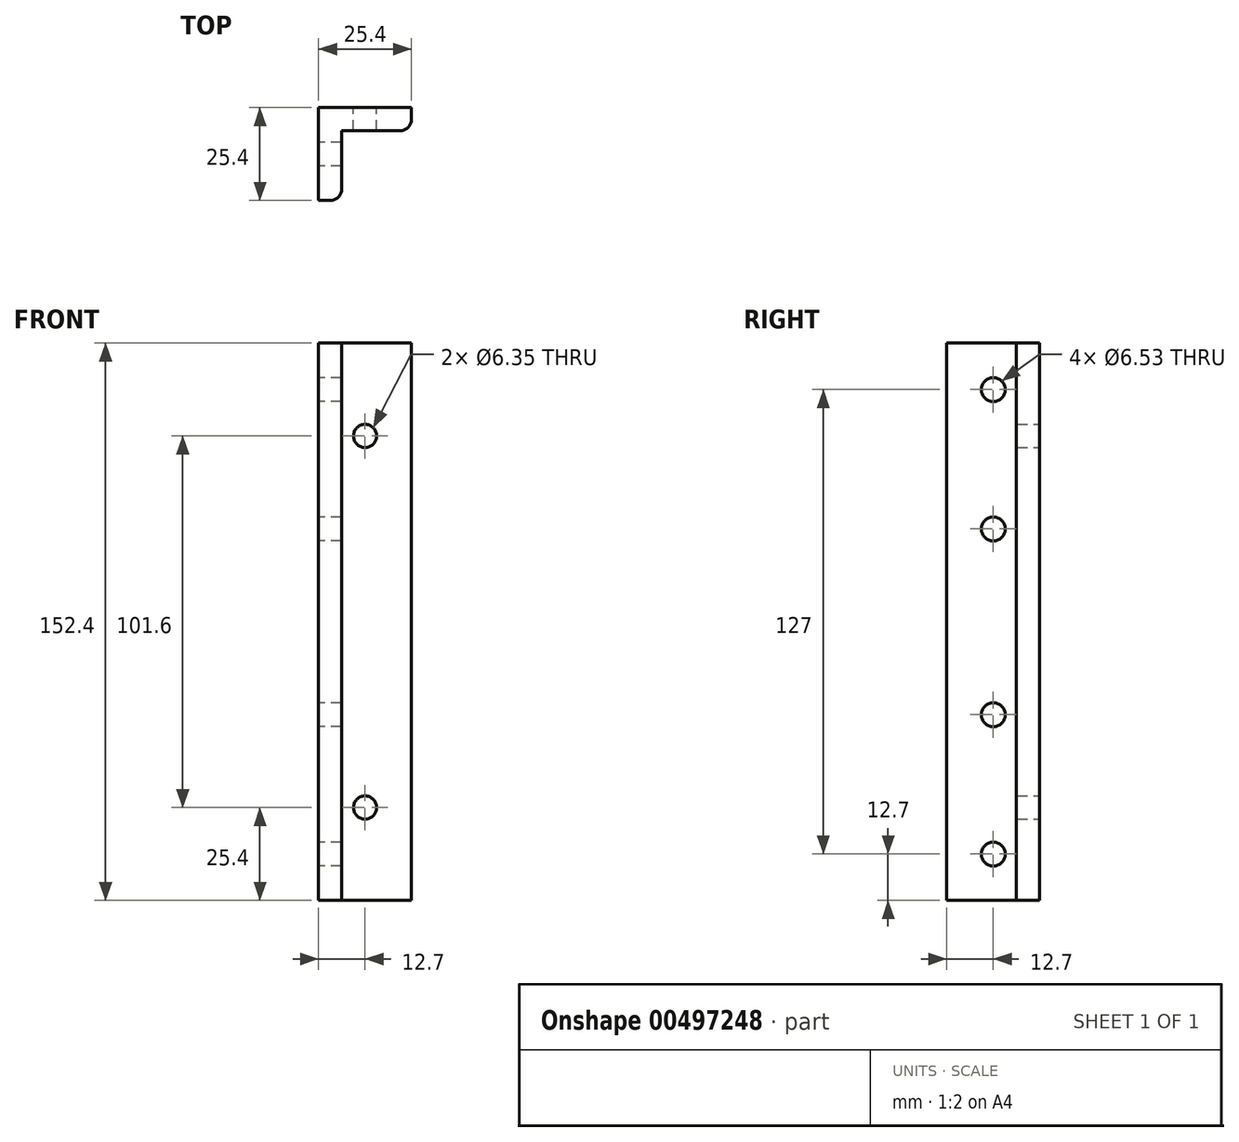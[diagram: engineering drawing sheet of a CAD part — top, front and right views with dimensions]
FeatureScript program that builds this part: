
annotation { "Feature Type Name" : "Feature", "Feature Type Description" : "" }
export const myFeature = defineFeature(function(context is Context, id is Id, definition is map)
    precondition{}
    {
        {
            var Q0;
            Q0=qCreatedBy(makeId("Top.planeOp"),FACE);
            var sketch = newSketch(context, id + "F0", { "sketchPlane" : qUnion([Q0])});
            skLineSegment(sketch, "E0", {"start": v(0, 0) * mm, "end": v(25.4, 0) * mm});
            skLineSegment(sketch, "E1", {"start": v(0, 0) * mm, "end": v(0, -25.4) * mm});
            skLineSegment(sketch, "E2", {"start": v(6.35, -19.05) * mm, "end": v(6.35, -6.35) * mm});
            skLineSegment(sketch, "E3", {"start": v(6.35, -6.35) * mm, "end": v(18.93, -6.35) * mm});
            skLineSegment(sketch, "E4", {"start": v(0, -25.4) * mm, "end": v(3.18, -25.4) * mm});
            skLineSegment(sketch, "E5", {"start": v(6.35, -22.23) * mm, "end": v(6.35, -19.05) * mm});
            skArc(sketch, "E6", {"start": v(3.18, -25.4) * mm, "mid": v(5.42, -24.47) * mm, "end": v(6.35, -22.23) * mm});
            skLineSegment(sketch, "E7", {"start": v(19.17, -6.35) * mm, "end": v(22.23, -6.35) * mm});
            skLineSegment(sketch, "E8", {"start": v(25.4, -3.17) * mm, "end": v(25.4, 0) * mm});
            skArc(sketch, "E9.trimOffspring", {"start": v(25.4, 0) * mm, "mid": v(25.4, 0) * mm, "end": v(25.4, 0) * mm});
            skLineSegment(sketch, "E10", {"start": v(18.93, -6.35) * mm, "end": v(19.17, -6.35) * mm});
            skArc(sketch, "E11", {"start": v(22.23, -6.35) * mm, "mid": v(24.47, -5.42) * mm, "end": v(25.4, -3.17) * mm});
            skPoint(sketch, "E12.orphan", {"position": v(6.35, -25.4) * mm});
            skPoint(sketch, "E13.orphan", {"position": v(25.4, -6.35) * mm});
            skSolve(sketch);
        }
        {
            var Q0;
            Q0 = qSketchRegion(id + "F0", true);
            extrude(context, id + "F1", {"entities" : qUnion([Q0]), "depth" : 152.4 * mm});
        }
        {
            var Q0;
            Q0=makeQuery(id+"F1.opExtrude","SWEPT_FACE",FACE,{"disambiguationData":[OSD([sQuery(id+"F0.wireOp",EDGE,"E1")])]});
            var sketch = newSketch(context, id + "F2", { "sketchPlane" : qUnion([Q0])});
            skPoint(sketch, "E14", {"position": v(12.7, 139.7) * mm});
            skPoint(sketch, "E15", {"position": v(12.7, 12.7) * mm});
            skPoint(sketch, "E16", {"position": v(12.7, 50.8) * mm});
            skPoint(sketch, "E17", {"position": v(12.7, 101.6) * mm});
            skSolve(sketch);
        }
        {
            var Q0;
            Q0=makeQuery(id+"F1.opExtrude","SWEPT_FACE",FACE,{"disambiguationData":[OSD([sQuery(id+"F0.wireOp",EDGE,"E0")])]});
            var sketch = newSketch(context, id + "F3", { "sketchPlane" : qUnion([Q0])});
            skPoint(sketch, "E18", {"position": v(-12.7, 127) * mm});
            skPoint(sketch, "E19", {"position": v(-12.7, 25.4) * mm});
            skSolve(sketch);
        }
        {
            var Q0;
            Q0=sQuery(id+"F3.wireOp",VERTEX,"E18");
            var Q1;
            Q1=sQuery(id+"F3.wireOp",VERTEX,"E19");
            var Q2;
            Q2=makeQuery(id+"F1.opExtrude","SWEPT_BODY",BODY,{"disambiguationData":[OSD([sQuery(id+"F0.wireOp",EDGE,"E0"),sQuery(id+"F0.wireOp",EDGE,"E1"),sQuery(id+"F0.wireOp",EDGE,"E2"),sQuery(id+"F0.wireOp",EDGE,"E3"),sQuery(id+"F0.wireOp",EDGE,"E4"),sQuery(id+"F0.wireOp",EDGE,"E5"),sQuery(id+"F0.wireOp",EDGE,"E6"),sQuery(id+"F0.wireOp",EDGE,"E7"),sQuery(id+"F0.wireOp",EDGE,"E8"),sQuery(id+"F0.wireOp",EDGE,"E9.trimOffspring"),sQuery(id+"F0.wireOp",EDGE,"E10"),sQuery(id+"F0.wireOp",EDGE,"E11")])]});
            hole(context, id + "F4", {"style" : HoleStyle.SIMPLE, "endStyle" : HoleEndStyle.BLIND, "holeDiameter" : 6.35 * mm, "holeDepth" : 25.4 * mm, "isTappedThrough" : true, "tappedDepth" : 12.7 * mm, "tapClearance" : 3, "startFromSketch" : true, "locations" : qUnion([Q0, Q1]), "scope" : qUnion([Q2])});
        }
        {
            var Q0;
            Q0=sQuery(id+"F2.wireOp",VERTEX,"E15");
            var Q1;
            Q1=sQuery(id+"F2.wireOp",VERTEX,"E16");
            var Q2;
            Q2=sQuery(id+"F2.wireOp",VERTEX,"E17");
            var Q3;
            Q3=sQuery(id+"F2.wireOp",VERTEX,"E14");
            var Q4;
            Q4=makeQuery(id+"F1.opExtrude","SWEPT_BODY",BODY,{"disambiguationData":[OSD([sQuery(id+"F0.wireOp",EDGE,"E0"),sQuery(id+"F0.wireOp",EDGE,"E1"),sQuery(id+"F0.wireOp",EDGE,"E2"),sQuery(id+"F0.wireOp",EDGE,"E3"),sQuery(id+"F0.wireOp",EDGE,"E4"),sQuery(id+"F0.wireOp",EDGE,"E5"),sQuery(id+"F0.wireOp",EDGE,"E6"),sQuery(id+"F0.wireOp",EDGE,"E7"),sQuery(id+"F0.wireOp",EDGE,"E8"),sQuery(id+"F0.wireOp",EDGE,"E9.trimOffspring"),sQuery(id+"F0.wireOp",EDGE,"E10"),sQuery(id+"F0.wireOp",EDGE,"E11")])]});
            hole(context, id + "F5", {"style" : HoleStyle.SIMPLE, "endStyle" : HoleEndStyle.BLIND, "holeDiameter" : 6.53 * mm, "holeDepth" : 25.4 * mm, "isTappedThrough" : true, "tappedDepth" : 12.7 * mm, "tapClearance" : 3, "startFromSketch" : true, "locations" : qUnion([Q0, Q1, Q2, Q3]), "scope" : qUnion([Q4])});
        }
    });
